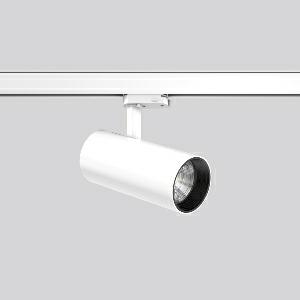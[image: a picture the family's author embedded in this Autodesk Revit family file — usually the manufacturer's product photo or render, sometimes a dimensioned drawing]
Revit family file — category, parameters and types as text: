
# Revit family: deecos_s_mini_742201_002_3_6892
name_source: partatom
category: Lighting Fixtures
units: mm (PartAtom-declared; Revit-internal decimal feet)

## family parameters
Cut with Voids When Loaded = No
Host = Face
Light Source = No
Part Type = Normal
Room Calculation Point = No
Round Connector Dimension = Use Diameter
Shared = No

## types (1)
- DEECOS S mini (1 x LED Modul 935, 2300 lm, 3500)
    Apparent Load = 20 VA
    Approval mark = CE
    CIE Flux Codes = 80 99 100 100 100
    Color Rendering = 92
    Color Temperature = 3500
    Default Elevation = 1800 mm
    Description = Series: DEECOS S mini
LED surface-mounted projector in modern design with no visible cooling ribs. Housing: die-cast aluminium, powder-coated. Rotation range: 356°. Swivel range: 90°. Black plastic ring and recessed LED to prevent glare from the side. Optical assembly with lens made of plastic (polycarbonate) for the best homogeneous light distribution - can be changed without tools. Best colour rendering index Ra>90. With multi adaptor for 3-circuit tracks 230 V. Suitable for Track on ceiling, Wall track. High quality converter without flickering and stroboscopic effect. The following accessories can be mounted without use of tools: interchangeable lenses, decorative glasses, honeycomb louvre, clear and frosted diffusers, white interchangeable plastic ring. 
Colour: traffic white, matt (RAL 9016)
Diameter: 87 mm
Height: 214 mm
Lamp: LED
Socket: without socket
Colour temperature: 3500K
Colour rendering index (CRI): 92
System power: 20 W
Rated luminous flux: 2300 lm
Luminous efficiency: 115 lm/W
Control gear: Regulated power supply
Protection class: I
Type of protection: IP 20
    Height = 214 mm
    Lamp = 1 x LED Modul 935
    Lamp Light Flux = 2300 lm
    Lamp count = 1
    Length = 87 mm
    Lifetime = 50000 h
    Luminous efficacy = 115 lm/W
    Manufacturer = RZB
    ModVariant = No
    Model = 742201.002.3
    Mounting Place = Ceiling
    Mounting Type = Rail mounted
    Number of Poles = 1
    OnlyDefault = Yes
    Power Factor = 1
    Product Name = DEECOS S mini
    Product group = Track mounted projectors
    ProductGroupID = 301
    Protection Class = Protection class I
    Protection Degree = IP 20
    RLX_Detail_Level = 1
    RLX_Emergency_Light_Flux = 0 lm
    RLX_Emergency_Type = 0
    RLX_Emergency_Type_DB = No
    RlxData = <blob elided: 35473 chars, md5=d1e639a4>
    Socket = socket
    Standby Power = 0 W
    System Light Flux = 2300 lm
    System Power = 20 W
    Type Comments = Product without accessories
    Type Image = 741930.002.jpg
    URL = http://relux.com
    VarID = ---
    Voltage = 230 V
    Voltage Range = 220-240 V
    Weight = 0.00 kg
    Width = 0 mm  [stored 0 ft]

note: [stored X ft] marks values corroborated as IEEE doubles in the binary element streams (Revit-internal decimal feet)

## geometry (parser evidence)
native form markers: Blend x4, Sweep x13
no freeform markers — native parametric forms only
